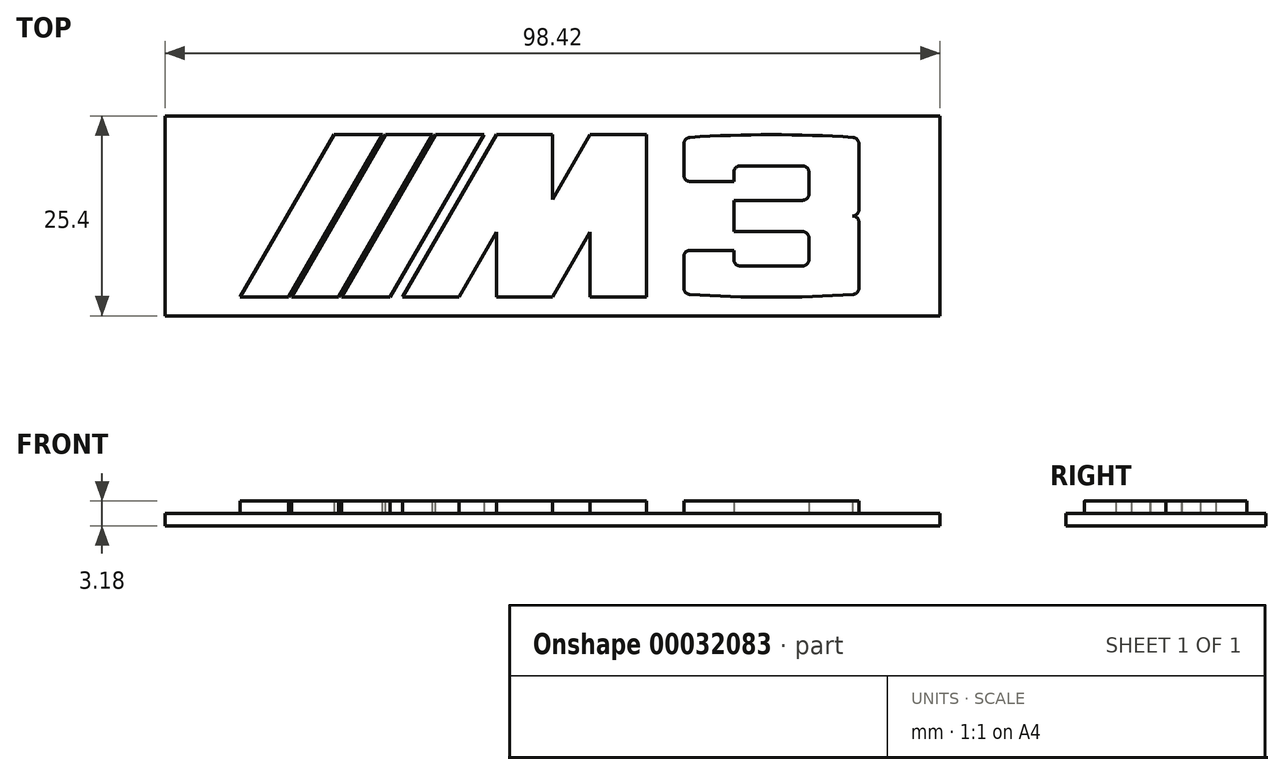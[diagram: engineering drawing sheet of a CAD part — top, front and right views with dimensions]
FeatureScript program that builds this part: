
annotation { "Feature Type Name" : "Feature", "Feature Type Description" : "" }
export const myFeature = defineFeature(function(context is Context, id is Id, definition is map)
    precondition{}
    {
        {
            var Q0;
            Q0=qCreatedBy(makeId("Front.planeOp"),FACE);
            var sketch = newSketch(context, id + "F0", { "sketchPlane" : qUnion([Q0])});
            skLineSegment(sketch, "E0.bottom", {"start": v(0, 0) * mm, "end": v(98.43, 0) * mm});
            skLineSegment(sketch, "E0.top", {"start": v(0, 25.4) * mm, "end": v(98.43, 25.4) * mm});
            skLineSegment(sketch, "E0.left", {"start": v(0, 0) * mm, "end": v(0, 25.4) * mm});
            skLineSegment(sketch, "E0.right", {"start": v(98.43, 0) * mm, "end": v(98.43, 25.4) * mm});
            skSolve(sketch);
        }
        {
            var Q0;
            Q0=makeQuery(id+"F0.imprint","IMPRINT",FACE,{"disambiguationData":[TD([[makeQuery(id+"F0.imprint","IMPRINT",EDGE,{"derivedFrom":sQuery(id+"F0.wireOp",EDGE,"E0.bottom")}),1.0]])]});
            extrude(context, id + "F1", {"entities" : qUnion([Q0]), "depth" : 1.59 * mm});
        }
        {
            var Q0;
            Q0=makeQuery(id+"F1.opExtrude","CAP_FACE",FACE,{"disambiguationData":[OSD([sQuery(id+"F0.wireOp",EDGE,"E0.bottom"),sQuery(id+"F0.wireOp",EDGE,"E0.top"),sQuery(id+"F0.wireOp",EDGE,"E0.left"),sQuery(id+"F0.wireOp",EDGE,"E0.right")])],"isStart":false});
            var sketch = newSketch(context, id + "F2", { "sketchPlane" : qUnion([Q0])});
            skLineSegment(sketch, "E1", {"start": v(0, 2.38) * mm, "end": v(98.43, 2.38) * mm, "construction": true});
            skLineSegment(sketch, "E2", {"start": v(0, 23.02) * mm, "end": v(98.43, 23.02) * mm, "construction": true});
            skLineSegment(sketch, "E3", {"start": v(9.53, 2.38) * mm, "end": v(21.44, 23.02) * mm});
            skLineSegment(sketch, "E4", {"start": v(21.44, 23.02) * mm, "end": v(40.5, 23.02) * mm});
            skLineSegment(sketch, "E5", {"start": v(40.5, 23.02) * mm, "end": v(28.58, 2.38) * mm});
            skLineSegment(sketch, "E6", {"start": v(28.58, 2.38) * mm, "end": v(9.53, 2.38) * mm});
            skLineSegment(sketch, "E7", {"start": v(30.16, 2.38) * mm, "end": v(42.08, 23.02) * mm});
            skLineSegment(sketch, "E8", {"start": v(42.08, 23.02) * mm, "end": v(49.22, 23.02) * mm});
            skLineSegment(sketch, "E9", {"start": v(49.22, 23.02) * mm, "end": v(49.22, 14.75) * mm});
            skLineSegment(sketch, "E10", {"start": v(49.22, 14.75) * mm, "end": v(54, 23.02) * mm});
            skLineSegment(sketch, "E11", {"start": v(54, 23.02) * mm, "end": v(61.14, 23.02) * mm});
            skLineSegment(sketch, "E12", {"start": v(61.14, 23.02) * mm, "end": v(61.14, 2.38) * mm});
            skLineSegment(sketch, "E13", {"start": v(61.14, 2.38) * mm, "end": v(54, 2.38) * mm});
            skLineSegment(sketch, "E14", {"start": v(54, 2.38) * mm, "end": v(54, 10.65) * mm});
            skLineSegment(sketch, "E15", {"start": v(54, 10.65) * mm, "end": v(49.22, 2.38) * mm});
            skLineSegment(sketch, "E16", {"start": v(49.22, 2.38) * mm, "end": v(42.08, 2.38) * mm});
            skLineSegment(sketch, "E17", {"start": v(42.08, 2.38) * mm, "end": v(42.08, 10.65) * mm});
            skLineSegment(sketch, "E18", {"start": v(42.08, 10.65) * mm, "end": v(37.3, 2.38) * mm});
            skLineSegment(sketch, "E19", {"start": v(37.3, 2.38) * mm, "end": v(30.16, 2.38) * mm});
            skLineSegment(sketch, "E20.left", {"start": v(65.9, 21.88) * mm, "end": v(65.9, 17.86) * mm});
            skLineSegment(sketch, "E20.right", {"start": v(88.12, 21.88) * mm, "end": v(88.12, 16.87) * mm});
            skPoint(sketch, "E21.visualSharp", {"position": v(65.9, 23.02) * mm});
            skPoint(sketch, "E22.visualSharp", {"position": v(65.9, 2.38) * mm});
            skPoint(sketch, "E23.visualSharp", {"position": v(88.12, 2.38) * mm});
            skLineSegment(sketch, "E24", {"start": v(87.33, 23.02) * mm, "end": v(87.33, 2.38) * mm, "construction": true});
            skPoint(sketch, "E25", {"position": v(87.33, 12.7) * mm});
            skArc(sketch, "E26", {"start": v(87.33, 12.7) * mm, "mid": v(87.9, 12.93) * mm, "end": v(88.12, 13.5) * mm});
            skArc(sketch, "E27", {"start": v(88.12, 11.9) * mm, "mid": v(87.9, 12.47) * mm, "end": v(87.33, 12.7) * mm});
            skLineSegment(sketch, "E28", {"start": v(65.9, 12.7) * mm, "end": v(88.12, 12.7) * mm, "construction": true});
            skLineSegment(sketch, "E29", {"start": v(66.7, 17.07) * mm, "end": v(72.25, 17.07) * mm});
            skLineSegment(sketch, "E30", {"start": v(66.7, 8.33) * mm, "end": v(72.25, 8.33) * mm});
            skLineSegment(sketch, "E31", {"start": v(72.25, 17.07) * mm, "end": v(72.25, 18.26) * mm});
            skLineSegment(sketch, "E32", {"start": v(73.04, 19.05) * mm, "end": v(80.98, 19.05) * mm});
            skLineSegment(sketch, "E33", {"start": v(81.77, 18.26) * mm, "end": v(81.77, 15.48) * mm});
            skLineSegment(sketch, "E34", {"start": v(80.98, 14.68) * mm, "end": v(72.25, 14.68) * mm});
            skLineSegment(sketch, "E35", {"start": v(72.25, 14.68) * mm, "end": v(72.25, 10.72) * mm});
            skLineSegment(sketch, "E36", {"start": v(72.25, 10.72) * mm, "end": v(80.98, 10.72) * mm});
            skLineSegment(sketch, "E37", {"start": v(81.77, 9.92) * mm, "end": v(81.77, 7.14) * mm});
            skLineSegment(sketch, "E38", {"start": v(80.98, 6.35) * mm, "end": v(73.04, 6.35) * mm});
            skLineSegment(sketch, "E39", {"start": v(72.25, 7.14) * mm, "end": v(72.25, 8.33) * mm});
            skLineSegment(sketch, "E40", {"start": v(81.77, 16.87) * mm, "end": v(88.12, 16.87) * mm, "construction": true});
            skLineSegment(sketch, "E41.trimOffspring", {"start": v(65.9, 7.54) * mm, "end": v(65.9, 3.52) * mm});
            skArc(sketch, "E42", {"start": v(66.64, 2.73) * mm, "mid": v(77.01, 2.38) * mm, "end": v(87.38, 2.73) * mm});
            skArc(sketch, "E43", {"start": v(87.38, 22.67) * mm, "mid": v(77.01, 23.02) * mm, "end": v(66.64, 22.67) * mm});
            skPoint(sketch, "E44.visualSharp", {"position": v(88.12, 22.62) * mm});
            skArc(sketch, "E44.filletArc", {"start": v(88.12, 21.88) * mm, "mid": v(87.9, 22.42) * mm, "end": v(87.38, 22.67) * mm});
            skPoint(sketch, "E45.visualSharp", {"position": v(65.9, 22.62) * mm});
            skArc(sketch, "E45.filletArc", {"start": v(66.64, 22.67) * mm, "mid": v(66.11, 22.42) * mm, "end": v(65.9, 21.88) * mm});
            skPoint(sketch, "E46.visualSharp", {"position": v(65.9, 17.07) * mm});
            skArc(sketch, "E46.filletArc", {"start": v(65.9, 17.86) * mm, "mid": v(66.13, 17.3) * mm, "end": v(66.7, 17.07) * mm});
            skPoint(sketch, "E47.visualSharp", {"position": v(65.9, 8.33) * mm});
            skArc(sketch, "E47.filletArc", {"start": v(66.7, 8.33) * mm, "mid": v(66.13, 8.1) * mm, "end": v(65.9, 7.54) * mm});
            skPoint(sketch, "E48.visualSharp", {"position": v(65.9, 2.78) * mm});
            skArc(sketch, "E48.filletArc", {"start": v(65.9, 3.52) * mm, "mid": v(66.11, 2.98) * mm, "end": v(66.64, 2.73) * mm});
            skPoint(sketch, "E49.visualSharp", {"position": v(88.12, 2.78) * mm});
            skArc(sketch, "E49.filletArc", {"start": v(87.38, 2.73) * mm, "mid": v(87.9, 2.98) * mm, "end": v(88.12, 3.52) * mm});
            skPoint(sketch, "E50.visualSharp", {"position": v(72.25, 19.05) * mm});
            skArc(sketch, "E50.filletArc", {"start": v(73.04, 19.05) * mm, "mid": v(72.48, 18.82) * mm, "end": v(72.25, 18.26) * mm});
            skPoint(sketch, "E51.visualSharp", {"position": v(81.77, 19.05) * mm});
            skArc(sketch, "E51.filletArc", {"start": v(81.77, 18.26) * mm, "mid": v(81.54, 18.82) * mm, "end": v(80.98, 19.05) * mm});
            skPoint(sketch, "E52.visualSharp", {"position": v(81.77, 14.68) * mm});
            skArc(sketch, "E52.filletArc", {"start": v(80.98, 14.68) * mm, "mid": v(81.54, 14.92) * mm, "end": v(81.77, 15.48) * mm});
            skPoint(sketch, "E53.visualSharp", {"position": v(81.77, 10.72) * mm});
            skArc(sketch, "E53.filletArc", {"start": v(81.77, 9.92) * mm, "mid": v(81.54, 10.48) * mm, "end": v(80.98, 10.72) * mm});
            skPoint(sketch, "E54.visualSharp", {"position": v(81.77, 6.35) * mm});
            skArc(sketch, "E54.filletArc", {"start": v(80.98, 6.35) * mm, "mid": v(81.54, 6.58) * mm, "end": v(81.77, 7.14) * mm});
            skPoint(sketch, "E55.visualSharp", {"position": v(72.25, 6.35) * mm});
            skArc(sketch, "E55.filletArc", {"start": v(72.25, 7.14) * mm, "mid": v(72.48, 6.58) * mm, "end": v(73.04, 6.35) * mm});
            skLineSegment(sketch, "E56", {"start": v(65.9, 12.7) * mm, "end": v(72.25, 12.7) * mm, "construction": true});
            skLineSegment(sketch, "E57.trimOffspring", {"start": v(88.12, 11.9) * mm, "end": v(88.12, 3.52) * mm});
            skLineSegment(sketch, "E58", {"start": v(88.12, 16.87) * mm, "end": v(88.12, 13.5) * mm});
            skSolve(sketch);
        }
        {
            var Q0;
            Q0=qSketchRegion(id+"F2",true);
            extrude(context, id + "F3", {"entities" : qUnion([Q0]), "operationType" : NewBodyOperationType.ADD, "depth" : 1.59 * mm});
        }
        {
            var Q0;
            Q0=makeQuery(id+"F3.opExtrude","CAP_FACE",FACE,{"disambiguationData":[OSD([sQuery(id+"F2.wireOp",EDGE,"E3"),sQuery(id+"F2.wireOp",EDGE,"E4"),sQuery(id+"F2.wireOp",EDGE,"E5"),sQuery(id+"F2.wireOp",EDGE,"E6")])],"isStart":false});
            var sketch = newSketch(context, id + "F4", { "sketchPlane" : qUnion([Q0])});
            skLineSegment(sketch, "E59", {"start": v(27.8, 23.02) * mm, "end": v(15.88, 2.38) * mm, "construction": true});
            skLineSegment(sketch, "E60", {"start": v(34.14, 23.02) * mm, "end": v(22.23, 2.38) * mm, "construction": true});
            skLineSegment(sketch, "E61", {"start": v(15.48, 12.7) * mm, "end": v(21.83, 12.7) * mm, "construction": true});
            skLineSegment(sketch, "E62", {"start": v(21.83, 12.7) * mm, "end": v(28.18, 12.7) * mm, "construction": true});
            skLineSegment(sketch, "E63", {"start": v(28.18, 12.7) * mm, "end": v(34.53, 12.7) * mm, "construction": true});
            skLineSegment(sketch, "E64", {"start": v(34.34, 23.02) * mm, "end": v(22.42, 2.38) * mm});
            skLineSegment(sketch, "E65", {"start": v(33.94, 23.02) * mm, "end": v(22.03, 2.38) * mm});
            skLineSegment(sketch, "E66", {"start": v(33.94, 23.02) * mm, "end": v(34.34, 23.02) * mm});
            skLineSegment(sketch, "E67", {"start": v(22.03, 2.38) * mm, "end": v(22.42, 2.38) * mm});
            skLineSegment(sketch, "E68", {"start": v(27.99, 23.02) * mm, "end": v(16.07, 2.38) * mm});
            skLineSegment(sketch, "E69", {"start": v(16.07, 2.38) * mm, "end": v(15.68, 2.38) * mm});
            skLineSegment(sketch, "E70", {"start": v(15.68, 2.38) * mm, "end": v(27.6, 23.02) * mm});
            skLineSegment(sketch, "E71", {"start": v(27.6, 23.02) * mm, "end": v(27.99, 23.02) * mm});
            skSolve(sketch);
        }
        {
            var Q0;
            Q0=qSketchRegion(id+"F4",true);
            var Q1;
            Q1=makeQuery(id+"F1.opExtrude","CAP_FACE",FACE,{"disambiguationData":[OSD([sQuery(id+"F0.wireOp",EDGE,"E0.bottom"),sQuery(id+"F0.wireOp",EDGE,"E0.top"),sQuery(id+"F0.wireOp",EDGE,"E0.left"),sQuery(id+"F0.wireOp",EDGE,"E0.right")])],"isStart":false});
            extrude(context, id + "F6", {"entities" : qUnion([Q0]), "operationType" : NewBodyOperationType.REMOVE, "endBound" : BoundingType.UP_TO_SURFACE, "oppositeDirection" : true, "endBoundEntityFace" : qUnion([Q1]), "depth" : 25.4 * mm});
        }
        {
            var Q0;
            Q0=makeQuery(id+"F1.opExtrude","SWEPT_BODY",BODY,{"disambiguationData":[OSD([sQuery(id+"F0.wireOp",EDGE,"E0.bottom"),sQuery(id+"F0.wireOp",EDGE,"E0.top"),sQuery(id+"F0.wireOp",EDGE,"E0.left"),sQuery(id+"F0.wireOp",EDGE,"E0.right")])]});
            var Q1;
            Q1=makeQuery(id+"F1.opExtrude","CAP_EDGE",EDGE,{"disambiguationData":[OSD([sQuery(id+"F0.wireOp",EDGE,"E0.bottom")])],"isStart":true});
            transform(context, id + "F5", {"entities" : qUnion([Q0]), "transformType" : TransformType.ROTATION, "transformAxis" : qUnion([Q1]), "angle" : 90 * degree, "oppositeDirection" : true, "makeCopy" : false});
        }
    });
